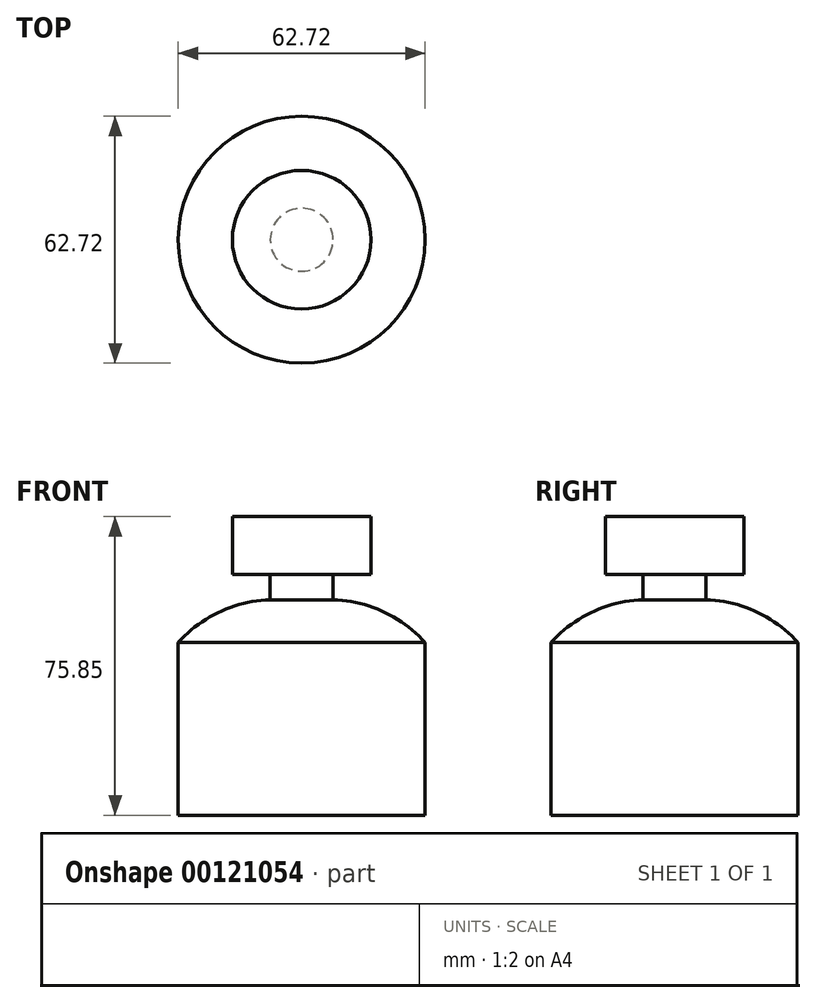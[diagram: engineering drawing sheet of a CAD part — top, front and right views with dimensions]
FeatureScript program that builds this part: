
annotation { "Feature Type Name" : "Feature", "Feature Type Description" : "" }
export const myFeature = defineFeature(function(context is Context, id is Id, definition is map)
    precondition{}
    {
        {
            var Q0;
            Q0=qCreatedBy(makeId("Front.planeOp"),FACE);
            var sketch = newSketch(context, id + "F0", { "sketchPlane" : qUnion([Q0])});
            skLineSegment(sketch, "E0", {"start": v(0, 46.72) * mm, "end": v(17.6, 46.72) * mm});
            skLineSegment(sketch, "E1", {"start": v(17.6, 32) * mm, "end": v(17.6, 46.72) * mm});
            skLineSegment(sketch, "E2", {"start": v(17.6, 32) * mm, "end": v(8, 32) * mm});
            skLineSegment(sketch, "E3", {"start": v(8, 32) * mm, "end": v(8, 25.6) * mm});
            skArc(sketch, "E4", {"start": v(31.36, 14.72) * mm, "mid": v(20.8, 22.55) * mm, "end": v(8, 25.6) * mm});
            skLineSegment(sketch, "E5", {"start": v(31.36, 14.72) * mm, "end": v(31.36, -29.13) * mm});
            skLineSegment(sketch, "E6", {"start": v(0, -29.13) * mm, "end": v(31.36, -29.13) * mm});
            skLineSegment(sketch, "E7", {"start": v(0, -29.13) * mm, "end": v(0, 46.72) * mm});
            skSolve(sketch);
        }
        {
            var Q0;
            Q0 = qSketchRegion(id + "F0", true);
            var Q1;
            Q1=sQuery(id+"F0.wireOp",EDGE,"E7");
            revolve(context, id + "F1", {"entities" : qUnion([Q0]), "axis" : qUnion([Q1]), "revolveType" : RevolveType.FULL});
        }
    });
